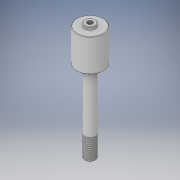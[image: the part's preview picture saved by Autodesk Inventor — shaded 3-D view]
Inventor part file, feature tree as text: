
AUTODESK INVENTOR PART (.ipt)
format: ipt  version: 2019 (Build 230136000, 136)  size: 146,432 bytes
history: native  units: mm
features: other x2, sketch x2, chamfer x1, hole x1
ambient origin geometry x8: Origin, YZ Plane, XZ Plane, XY Plane, X Axis, Y Axis, Z Axis, Center Point
bodies: Solide1 (feature_tree)
feature tree (6):
  other  "Révolution1"
  other  "Filetage2"
  chamfer  "Chanfrein1"  Distance=0.5mm
  hole  "Perçage2"  [1 undecoded]
  sketch  "Esquisse1"
  sketch  "Esquisse4"
note: 1 required parameter value undecoded (feature->parameter linkage not recoverable at this tier; creation-order binding heuristic only, values carry confidence <= 0.55)
